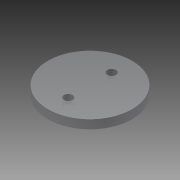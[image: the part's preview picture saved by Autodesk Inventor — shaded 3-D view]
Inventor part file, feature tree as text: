
AUTODESK INVENTOR PART (.ipt)
format: ipt  version: 2013 SP1 (Build 170176100, 176)  size: 83,456 bytes
history: native  units: mm
features: extrude x2, sketch x2
ambient origin geometry x8: Origin, YZ Plane, XZ Plane, XY Plane, X Axis, Y Axis, Z Axis, Center Point
bodies: Solid1 (feature_tree)
feature tree (4):
  extrude  "Extrusion1"  Depth=3.0mm TaperAngle=0.0deg
  extrude  "Extrusion4"  Depth=3.0mm
  sketch  "Sketch1"  dims[d0=29.0mm d3=3.0mm d4=0.0mm]
  sketch  "Sketch2"  dims[d22=9.5mm d31=3.0mm d33=3.0mm d34=15.0mm d35=7.5mm d36=10.0mm d37=0.0mm]
